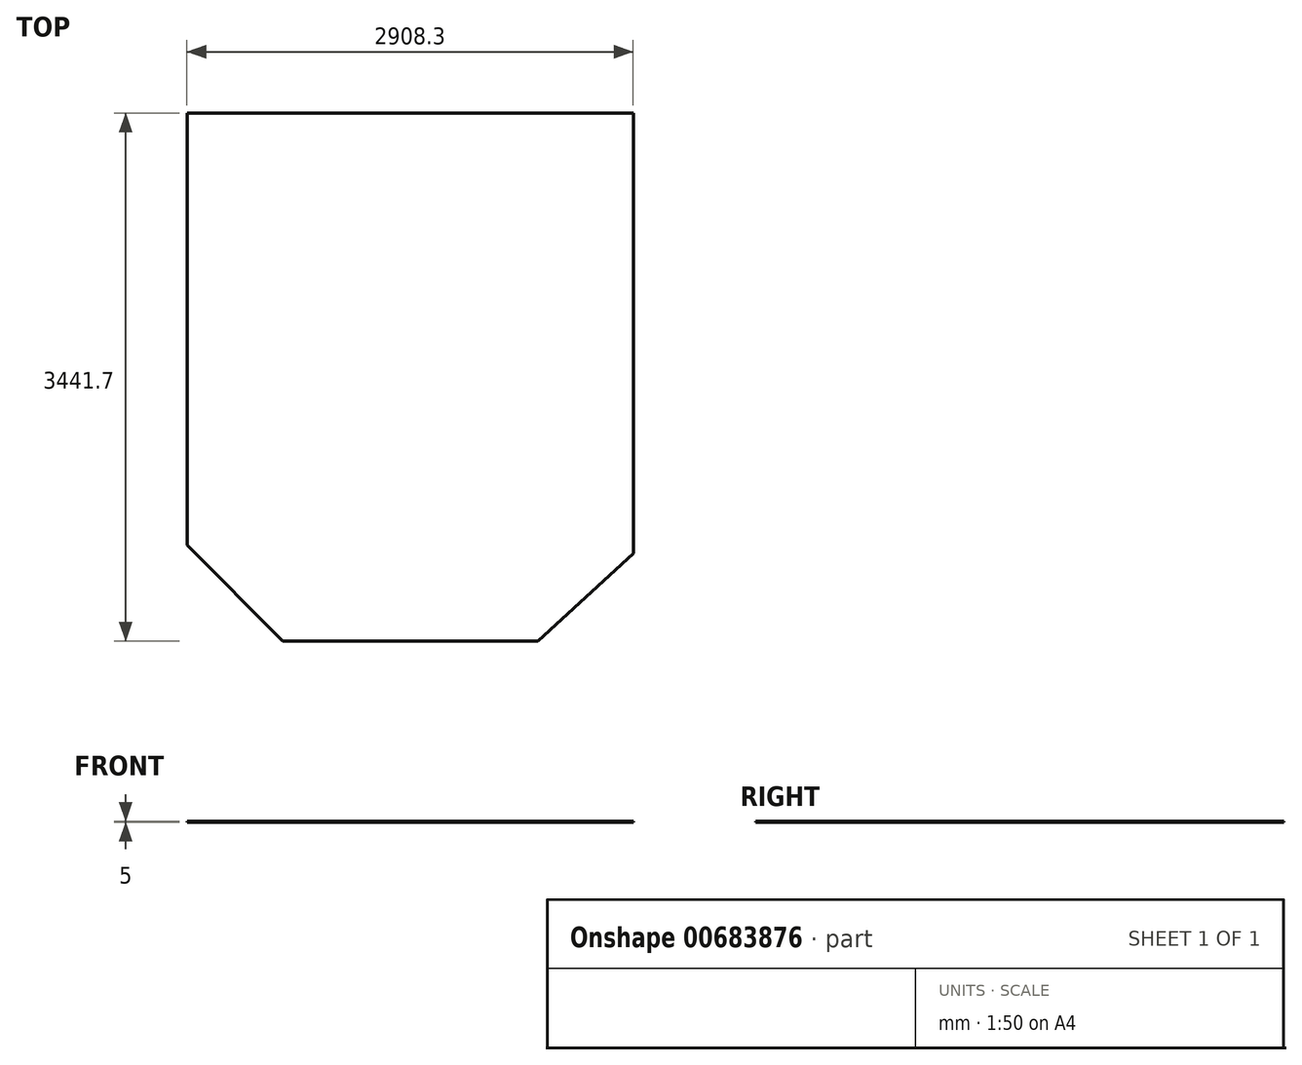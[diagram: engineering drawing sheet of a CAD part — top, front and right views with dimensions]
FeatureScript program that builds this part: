
annotation { "Feature Type Name" : "Feature", "Feature Type Description" : "" }
export const myFeature = defineFeature(function(context is Context, id is Id, definition is map)
    precondition{}
    {
        {
            var Q0;
            Q0=qCreatedBy(makeId("Top.planeOp"),FACE);
            var sketch = newSketch(context, id + "F0", { "sketchPlane" : qUnion([Q0])});
            skLineSegment(sketch, "E0.bottom", {"start": v(-1453.34, 1973.03) * mm, "end": v(1454.96, 1973.03) * mm});
            skLineSegment(sketch, "E0.top", {"start": v(-831.04, -1468.67) * mm, "end": v(832.66, -1468.67) * mm});
            skLineSegment(sketch, "E0.left", {"start": v(-1453.34, 1973.03) * mm, "end": v(-1453.34, -843.57) * mm});
            skLineSegment(sketch, "E0.right", {"start": v(1454.96, 1973.03) * mm, "end": v(1454.96, -897.17) * mm});
            skLineSegment(sketch, "E1", {"start": v(832.66, -1468.67) * mm, "end": v(1454.96, -897.17) * mm});
            skLineSegment(sketch, "E2", {"start": v(-831.04, -1468.67) * mm, "end": v(-1453.34, -843.57) * mm});
            skPoint(sketch, "E3.orphan", {"position": v(1454.96, -1468.67) * mm});
            skPoint(sketch, "E4.orphan", {"position": v(-1453.34, -1468.67) * mm});
            skSolve(sketch);
        }
        {
            var Q0;
            Q0 = qSketchRegion(id + "F0", true);
            extrude(context, id + "F1", {"entities" : qUnion([Q0]), "depth" : 5 * mm, "offsetDistance" : 25.4 * mm});
        }
    });
